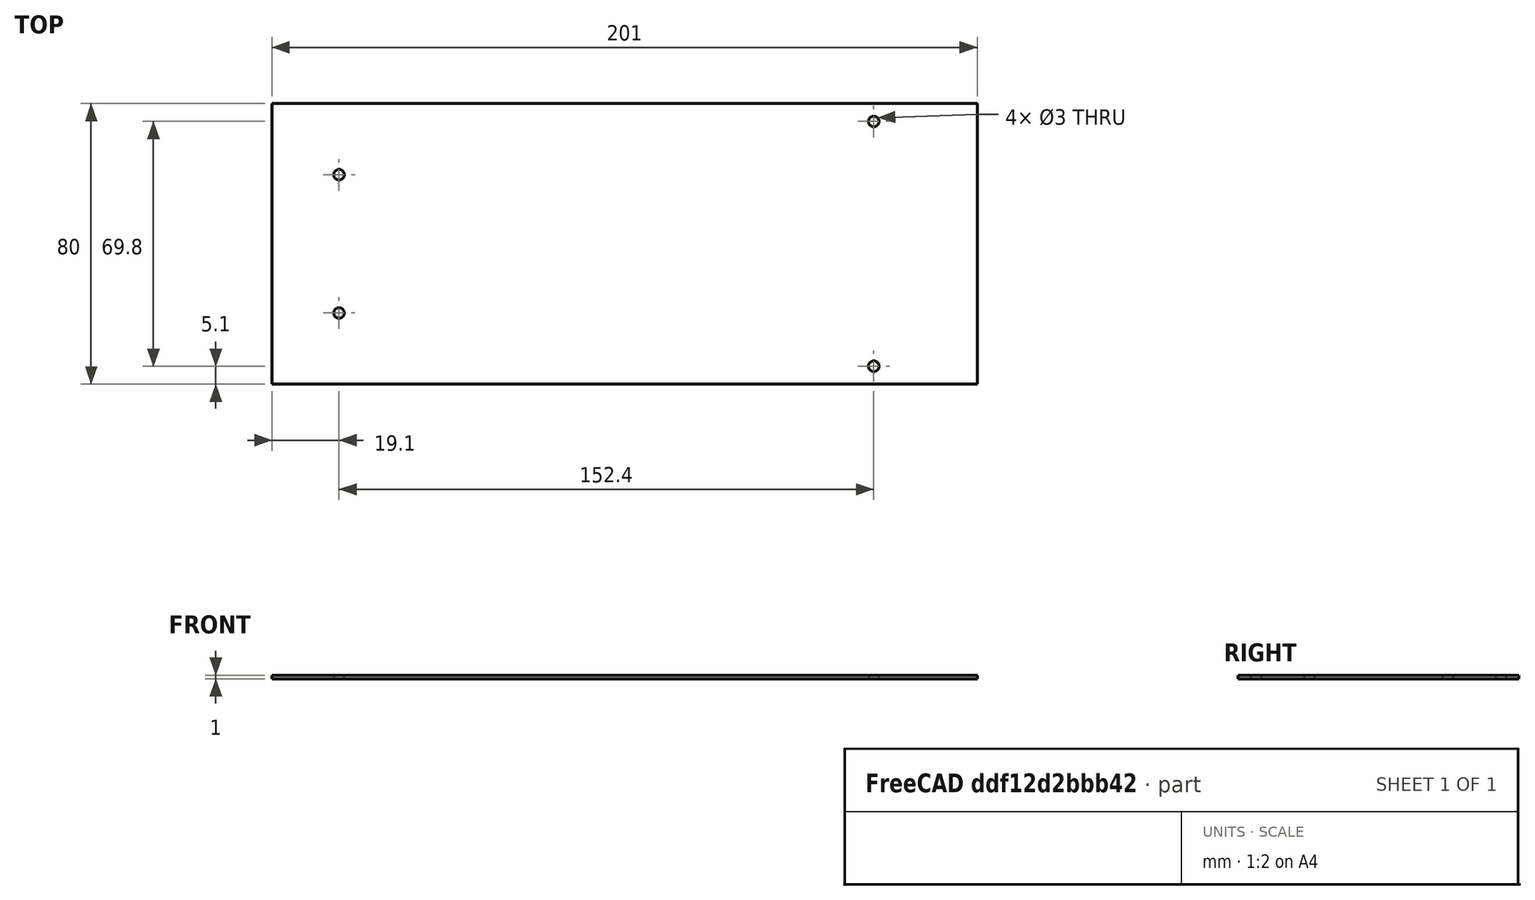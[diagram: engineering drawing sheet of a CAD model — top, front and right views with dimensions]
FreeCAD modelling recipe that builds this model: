
FCSTD DOCUMENT  (FreeCAD 1.0R38641 +468 (Git))
Label: doepfer_psu3
License: All rights reserved
LicenseURL: https://en.wikipedia.org/wiki/All_rights_reserved
objects: Sketcher::SketchObject×1, PartDesign::Pad×1, PartDesign::Body×1
note: 6 computed .brp shape members not serialized (recipe doc carries the construction recipe); baked Part::Feature solids carry a one-line shape summary decoded from their .brp

FEATURE [Sketcher::SketchObject] Sketch
  ArcFitTolerance = 1e-06
  AttachmentSupport = -> [XY_Plane]
  FullyConstrained = true
  MakeInternals = false
  MapMode = 5
  expr: Constraints[26] = 152.4
  sketch-geometry (10):
    g0: LineSegment StartX=0 StartY=0 StartZ=0 EndX=201 EndY=0 EndZ=0
    g1: LineSegment StartX=201 StartY=0 StartZ=0 EndX=201 EndY=80 EndZ=0
    g2: LineSegment StartX=201 StartY=80 StartZ=0 EndX=0 EndY=80 EndZ=0
    g3: LineSegment StartX=0 StartY=80 StartZ=0 EndX=0 EndY=0 EndZ=0
    g4: Circle CenterX=19.1 CenterY=59.7 CenterZ=0 NormalX=0 NormalY=0 NormalZ=1 AngleXU=0 Radius=1.5
    g5: Circle CenterX=19.1 CenterY=20.3 CenterZ=0 NormalX=0 NormalY=0 NormalZ=1 AngleXU=0 Radius=1.5
    g6: Circle CenterX=171.5 CenterY=74.9 CenterZ=0 NormalX=0 NormalY=0 NormalZ=1 AngleXU=0 Radius=1.5
    g7: Circle CenterX=171.5 CenterY=5.1 CenterZ=0 NormalX=0 NormalY=0 NormalZ=1 AngleXU=0 Radius=1.5
    g8: LineSegment [constr] StartX=19.1 StartY=20.3 StartZ=0 EndX=19.1 EndY=59.7 EndZ=0
    g9: LineSegment [constr] StartX=171.5 StartY=74.9 StartZ=0 EndX=171.5 EndY=5.1 EndZ=0
  constraints (29):
    c: Coincident(g0,g1)
    c: Coincident(g1,g2)
    c: Coincident(g2,g3)
    c: Coincident(g3,g0)
    c: Horizontal(g0)
    c: Horizontal(g2)
    c: Vertical(g1)
    c: Vertical(g3)
    c: Coincident(g0,g-1)
    c: DistanceY(g3,g3) = 80  'Height'
    c: DistanceX(g0,g0) = 201  'Width'
    c: DistanceY(g7,g6) = 69.8
    c: DistanceY(g5,g4) = 39.4
    c: DistanceX(g0,g5) = 19.1
    c: Coincident(g8,g5)
    c: Coincident(g8,g4)
    c: Coincident(g9,g6)
    c: Coincident(g9,g7)
    c: Vertical(g9)
    c: Vertical(g8)
    c: Diameter(g5) = 3  'PsuHoleDiameter'
    c: DistanceY(g0,g5) = 20.3
    c: Equal(g5,g4)
    c: Equal(g5,g7)
    c: Equal(g5,g6)
    c: DistanceY(g0,g7) = 5.1
    c: DistanceX(g5,g7) = 152.4
    c: DistanceY(g0,g6) = 74.9
    c: DistanceX(g0,g7) = 171.5
FEATURE [PartDesign::Pad] Pad
  Direction = (0,0,1)
  Length = 1
  Length2 = 10
  Profile = -> Sketch
  ReferenceAxis = -> Sketch [N_Axis]
  Refine = true
  Suppressed = false
  Type = 0
FEATURE [PartDesign::Body] Body  label="Psu"
  AllowCompound = false
  Group = -> [Sketch,Pad]
  Origin = -> Origin
  Tip = -> Pad
